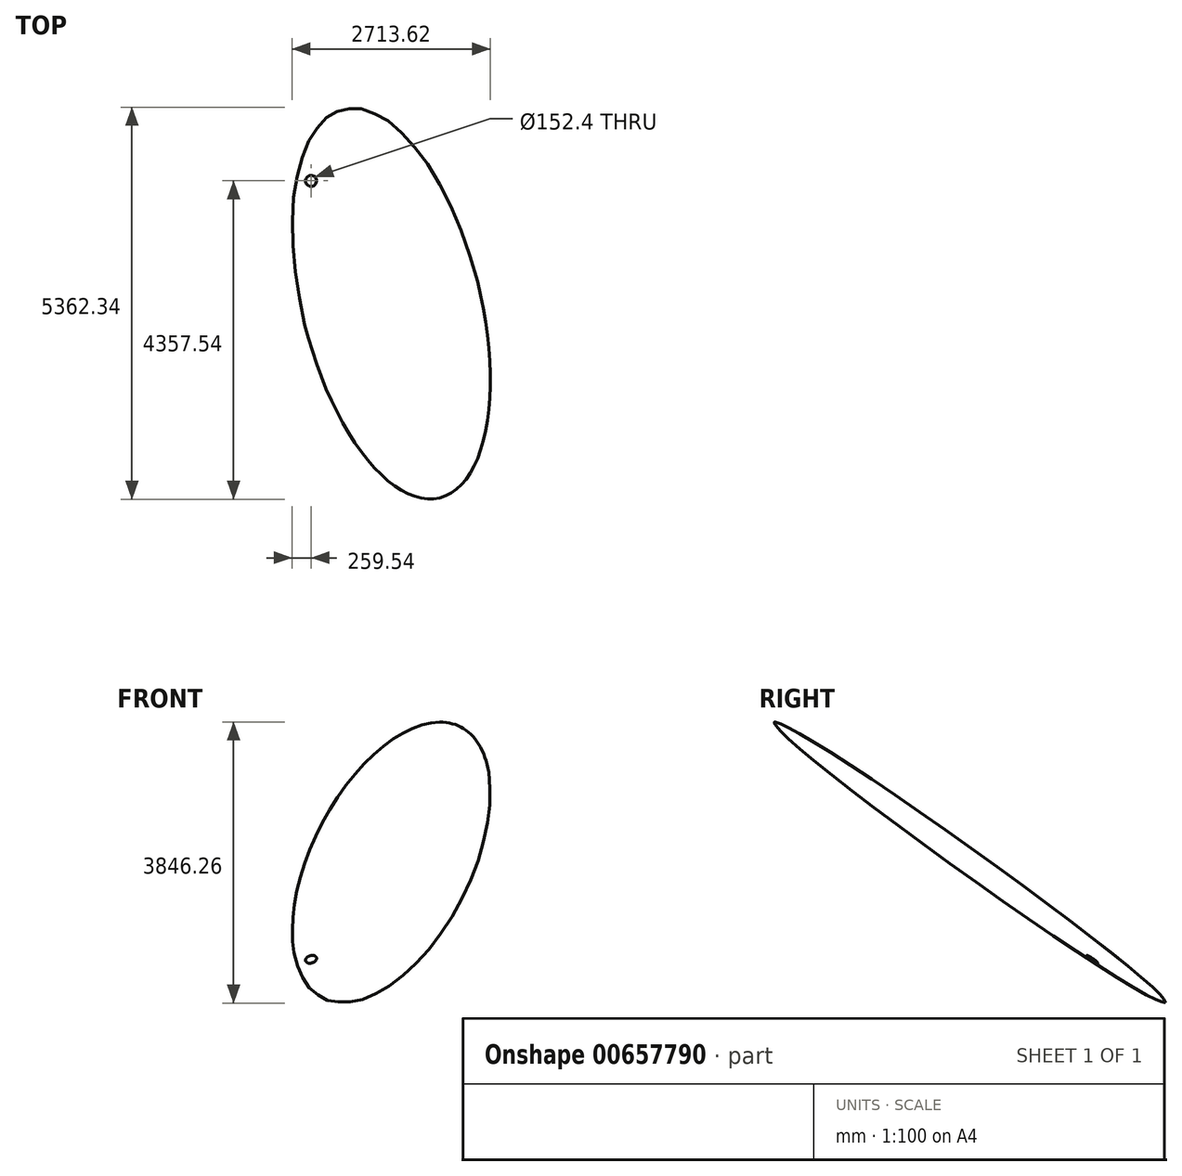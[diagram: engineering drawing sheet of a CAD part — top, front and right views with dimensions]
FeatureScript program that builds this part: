
annotation { "Feature Type Name" : "Feature", "Feature Type Description" : "" }
export const myFeature = defineFeature(function(context is Context, id is Id, definition is map)
    precondition{}
    {
        {
            assignVariable(context, id + "F0", {"name" : "Azimuth", "anyValue" : 256});
        }
        {
            assignVariable(context, id + "F1", {"name" : "Dip", "anyValue" : 35});
        }
        {
            assignVariable(context, id + "F2", {"name" : "Width", "anyValue" : .1});
        }
        {
            var Q0;
            Q0=qCreatedBy(makeId("Top.planeOp"),FACE);
            var sketch = newSketch(context, id + "F3", { "sketchPlane" : qUnion([Q0])});
            skEllipse(sketch, "E0", {"center": v(0, 0) * mm, "majorRadius": 1219.2 * mm, "minorRadius": 3352.8 * mm, "majorAxis": v(0, 1)});
            skLineSegment(sketch, "E1", {"start": v(0, 2286) * mm, "end": v(0, -2286) * mm, "construction": true});
            skLineSegment(sketch, "E2", {"start": v(-3977.64, 0) * mm, "end": v(3977.64, 0) * mm, "construction": true});
            skLineSegment(sketch, "E3.0", {"start": v(1097.28, 1219.2) * mm, "end": v(1097.28, -1219.2) * mm, "construction": true});
            skLineSegment(sketch, "E4.0", {"start": v(-3352.8, -1676.4) * mm, "end": v(3352.8, -1676.4) * mm, "construction": true});
            skSolve(sketch);
        }
        {
            var Q0;
            Q0=qCreatedBy(makeId("Top.planeOp"),FACE);
            var sketch = newSketch(context, id + "F4", { "sketchPlane" : qUnion([Q0])});
            skLineSegment(sketch, "E5", {"start": v(0, 0) * mm, "end": v(1097.28, 0) * mm});
            skLineSegment(sketch, "E6", {"start": v(1097.28, 0) * mm, "end": v(1097.28, -1676.4) * mm});
            skSolve(sketch);
        }
        {
            var Q0;
            Q0=qSketchRegion(id+"F3",true);
            extrude(context, id + "F5", {"entities" : qUnion([Q0]), "depth" : (getVariable(context, 'Width')) * mm});
        }
        {
            var Q0;
            Q0=qCreatedBy(makeId("Front.planeOp"),FACE);
            var sketch = newSketch(context, id + "F6", { "sketchPlane" : qUnion([Q0])});
            skLineSegment(sketch, "E7", {"start": v(0, 0) * mm, "end": v(0, -7924.8) * mm, "construction": true});
            skSolve(sketch);
        }
        {
            var Q0;
            Q0=makeQuery(id+"F5.opExtrude","SWEPT_BODY",BODY,{"disambiguationData":[OSD([sQuery(id+"F3.wireOp",EDGE,"E0"),sQuery(id+"F3.wireOp",EDGE,"TMMzbr5i-4nV4-ZnMr-aG6B-IGJ66UyS6uPJ")])]});
            var Q1;
            Q1=sQuery(id+"F3.wireOp",EDGE,"E1");
            transform(context, id + "F7", {"entities" : qUnion([Q0]), "transformType" : TransformType.ROTATION, "transformAxis" : qUnion([Q1]), "angle" : (getVariable(context, 'Dip')) * degree, "oppositeDirection" : true, "makeCopy" : false});
        }
        {
            var Q0;
            Q0=makeQuery(id+"F5.opExtrude","SWEPT_BODY",BODY,{"disambiguationData":[OSD([sQuery(id+"F3.wireOp",EDGE,"E0")])]});
            var Q1;
            Q1=sQuery(id+"F6.wireOp",EDGE,"E7");
            transform(context, id + "F8", {"entities" : qUnion([Q0]), "transformType" : TransformType.ROTATION, "transformAxis" : qUnion([Q1]), "angle" : (getVariable(context, 'Azimuth')) * degree, "makeCopy" : false});
        }
        {
            var Q0;
            Q0=makeQuery(id+"F5.opExtrude","SWEPT_BODY",BODY,{"disambiguationData":[OSD([sQuery(id+"F3.wireOp",EDGE,"E0"),sQuery(id+"F3.wireOp",EDGE,"TMMzbr5i-4nV4-ZnMr-aG6B-IGJ66UyS6uPJ")])]});
            var Q1;
            Q1=sQuery(id+"F4.wireOp",EDGE,"E5");
            transform(context, id + "F9", {"entities" : qUnion([Q0]), "transformType" : TransformType.TRANSLATION_ENTITY, "oppositeDirectionEntity" : false, "transformLine" : qUnion([Q1]), "makeCopy" : false});
        }
        {
            var Q0;
            Q0=makeQuery(id+"F5.opExtrude","SWEPT_BODY",BODY,{"disambiguationData":[OSD([sQuery(id+"F3.wireOp",EDGE,"E0"),sQuery(id+"F3.wireOp",EDGE,"TMMzbr5i-4nV4-ZnMr-aG6B-IGJ66UyS6uPJ")])]});
            var Q1;
            Q1=sQuery(id+"F4.wireOp",EDGE,"E6");
            transform(context, id + "F10", {"entities" : qUnion([Q0]), "transformType" : TransformType.TRANSLATION_ENTITY, "oppositeDirectionEntity" : false, "transformLine" : qUnion([Q1]), "makeCopy" : false});
        }
        {
            var Q0;
            Q0=qCreatedBy(makeId("Top.planeOp"),FACE);
            var sketch = newSketch(context, id + "F11", { "sketchPlane" : qUnion([Q0])});
            skCircle(sketch, "E8", {"center": v(0, 0) * mm, "radius": 76.2 * mm});
            skSolve(sketch);
        }
        {
            var Q0;
            Q0=qSketchRegion(id+"F11",true);
            extrude(context, id + "F12", {"entities" : qUnion([Q0]), "operationType" : NewBodyOperationType.REMOVE, "endBound" : BoundingType.THROUGH_ALL, "oppositeDirection" : true, "depth" : 30.48 * mm, "hasSecondDirection" : true, "secondDirectionBound" : SecondDirectionBoundingType.THROUGH_ALL, "secondDirectionOppositeDirection" : false, "secondDirectionDepth" : 30.48 * mm});
        }
        {
            var Q0;
            Q0=makeQuery(id+"F5.opExtrude","SWEPT_BODY",BODY,{"disambiguationData":[OSD([sQuery(id+"F3.wireOp",EDGE,"E0")])]});
            var Q1;
            Q1=sQuery(id+"F6.wireOp",EDGE,"E7");
            transform(context, id + "F13", {"entities" : qUnion([Q0]), "transformType" : TransformType.TRANSLATION_3D, "dx" : 0 * mm, "dy" : 0 * mm, "dz" : -6583.68 * mm, "makeCopy" : false});
        }
    });
